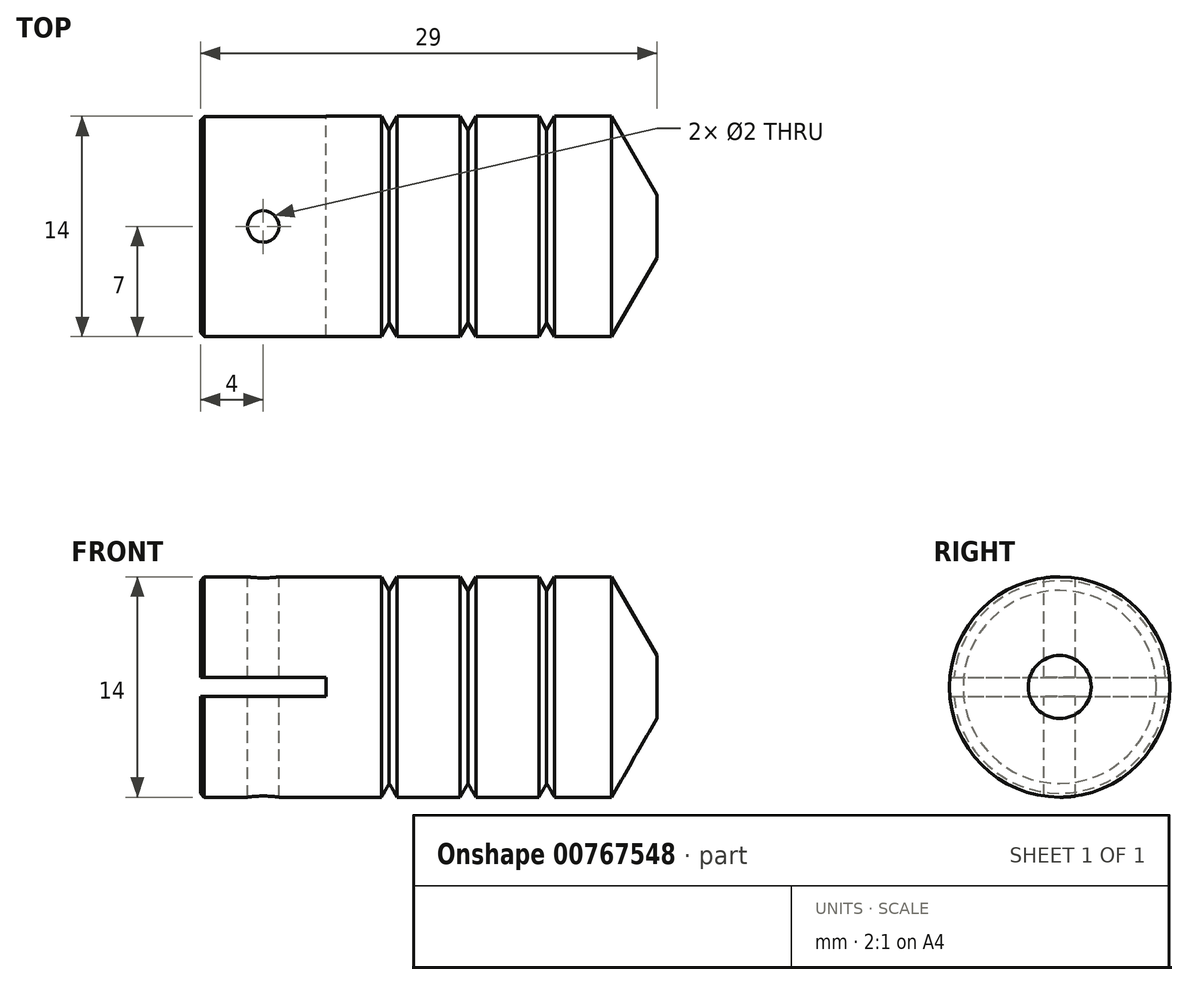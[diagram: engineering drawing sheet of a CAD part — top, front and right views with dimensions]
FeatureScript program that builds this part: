
annotation { "Feature Type Name" : "Feature", "Feature Type Description" : "" }
export const myFeature = defineFeature(function(context is Context, id is Id, definition is map)
    precondition{}
    {
        {
            var Q0;
            Q0=qCreatedBy(makeId("Front.planeOp"),FACE);
            var sketch = newSketch(context, id + "F0", { "sketchPlane" : qUnion([Q0])});
            skLineSegment(sketch, "E0", {"start": v(0, 0) * mm, "end": v(0, 7) * mm});
            skLineSegment(sketch, "E1", {"start": v(0, 7) * mm, "end": v(11.5, 7) * mm});
            skLineSegment(sketch, "E2", {"start": v(11.5, 7) * mm, "end": v(12, 6.13) * mm});
            skLineSegment(sketch, "E3", {"start": v(12, 6.13) * mm, "end": v(12.5, 7) * mm});
            skLineSegment(sketch, "E4", {"start": v(12.5, 7) * mm, "end": v(16.5, 7) * mm});
            skLineSegment(sketch, "E5", {"start": v(16.5, 7) * mm, "end": v(17, 6.13) * mm});
            skLineSegment(sketch, "E6", {"start": v(17, 6.13) * mm, "end": v(17.5, 7) * mm});
            skLineSegment(sketch, "E7", {"start": v(17.5, 7) * mm, "end": v(21.5, 7) * mm});
            skLineSegment(sketch, "E8", {"start": v(21.5, 7) * mm, "end": v(22, 6.13) * mm});
            skLineSegment(sketch, "E9", {"start": v(22, 6.13) * mm, "end": v(22.5, 7) * mm});
            skLineSegment(sketch, "E10", {"start": v(22.5, 7) * mm, "end": v(26.11, 7) * mm});
            skLineSegment(sketch, "E11", {"start": v(26.11, 7) * mm, "end": v(29, 2) * mm});
            skLineSegment(sketch, "E12", {"start": v(29, 2) * mm, "end": v(29, 0) * mm});
            skLineSegment(sketch, "E13", {"start": v(29, 0) * mm, "end": v(0, 0) * mm});
            skLineSegment(sketch, "E14", {"start": v(22, 6.13) * mm, "end": v(22, 7) * mm, "construction": true});
            skLineSegment(sketch, "E15", {"start": v(17, 6.13) * mm, "end": v(17, 7) * mm, "construction": true});
            skLineSegment(sketch, "E16", {"start": v(12, 6.13) * mm, "end": v(12, 7) * mm, "construction": true});
            skSolve(sketch);
        }
        {
            var Q0;
            Q0=makeQuery(id+"F0.imprint","IMPRINT",FACE,{"disambiguationData":[TD([[makeQuery(id+"F0.imprint","IMPRINT",EDGE,{"derivedFrom":sQuery(id+"F0.wireOp",EDGE,"E0")}),-1.0]])]});
            var Q1;
            Q1=sQuery(id+"F0.wireOp",EDGE,"E13");
            revolve(context, id + "F1", {"surfaceOperationType" : NewSurfaceOperationType.NEW, "entities" : qUnion([Q0]), "axis" : qUnion([Q1]), "revolveType" : RevolveType.FULL});
        }
        {
            var Q0;
            Q0=makeQuery(id+"F1.opRevolve","SWEPT_EDGE",EDGE,{"disambiguationData":[OSD([sQuery(id+"F0.wireOp",EDGE,"E0"),sQuery(id+"F0.wireOp",EDGE,"E1")])]});
            chamfer(context, id + "F2", {"entities" : qUnion([Q0]), "width" : 0.25 * mm, "tangentPropagation" : true});
        }
        {
            var Q0;
            Q0=qCreatedBy(makeId("Right.planeOp"),FACE);
            var sketch = newSketch(context, id + "F3", { "sketchPlane" : qUnion([Q0])});
            skLineSegment(sketch, "E17.bottom", {"start": v(-7.5, -0.6) * mm, "end": v(7.5, -0.6) * mm});
            skLineSegment(sketch, "E17.top", {"start": v(-7.5, 0.6) * mm, "end": v(7.5, 0.6) * mm});
            skLineSegment(sketch, "E17.left", {"start": v(-7.5, -0.6) * mm, "end": v(-7.5, 0.6) * mm});
            skLineSegment(sketch, "E17.right", {"start": v(7.5, -0.6) * mm, "end": v(7.5, 0.6) * mm});
            skPoint(sketch, "E17.middle", {"position": v(0, 0) * mm});
            skSolve(sketch);
        }
        {
            var Q0;
            Q0 = qSketchRegion(id + "F3", true);
            extrude(context, id + "F4", {"entities" : qUnion([Q0]), "operationType" : NewBodyOperationType.REMOVE, "depth" : 8 * mm, "offsetDistance" : 25 * mm});
        }
        {
            var Q0;
            Q0=qCreatedBy(makeId("Top.planeOp"),FACE);
            var sketch = newSketch(context, id + "F5", { "sketchPlane" : qUnion([Q0])});
            skCircle(sketch, "E18", {"center": v(4, 0) * mm, "radius": 1 * mm});
            skSolve(sketch);
        }
        {
            var Q0;
            Q0 = qSketchRegion(id + "F5", true);
            extrude(context, id + "F6", {"entities" : qUnion([Q0]), "operationType" : NewBodyOperationType.REMOVE, "endBound" : BoundingType.SYMMETRIC, "oppositeDirection" : true, "depth" : 25 * mm, "offsetDistance" : 25 * mm});
        }
    });
